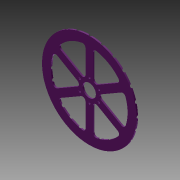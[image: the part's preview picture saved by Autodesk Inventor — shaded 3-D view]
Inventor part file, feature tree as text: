
AUTODESK INVENTOR PART (.ipt)
format: ipt  version: 2012 (Build 160160000, 160)  size: 259,072 bytes
history: native  units: in
note: dims shown in document units (in); Inventor stores cm internally (conversion verified against a paired STEP export)
features: extrude x4, sketch x4, pattern_circular x3, plane x1
ambient origin geometry x8: Origin, YZ Plane, XZ Plane, XY Plane, X Axis, Y Axis, Z Axis, Center Point
bodies: Solid1 (feature_tree)
feature tree (12):
  extrude  "Extrusion1"  Depth=1.125in
  extrude  "Extrusion6"  Depth=1.875in
  pattern_circular  "Circular Pattern4"  Count=6 Angle=360.0deg
  extrude  "Extrusion7"  Depth=0.75in
  pattern_circular  "Circular Pattern5"  [2 undecoded]
  plane  "Work Plane1"
  extrude  "Extrusion8"  Depth=0.3125in
  pattern_circular  "Circular Pattern6"  [2 undecoded]
  sketch  "Sketch1"  dims[d0=8.0in d1=1.125in]
  sketch  "Sketch6"  dims[d27=0.125in d28=0.0in d68=1.875in]
  sketch  "Sketch7"  dims[d69=0.1875in]
  sketch  "Sketch8"  dims[d70=0.1875in d71=0.0in d72=2.3622in d73=360.0deg d75=0.75in d76=0.25in d78=0.3125in d79=0.1875in d80=0.0in d81=2.3622in d82=360.0deg d84=0.25in d85=0.0625in d86=1.5in d87=0.0in d88=9.4488in d89=360.0deg]
note: 4 required parameter values undecoded (feature->parameter linkage not recoverable at this tier; creation-order binding heuristic only, values carry confidence <= 0.55)
